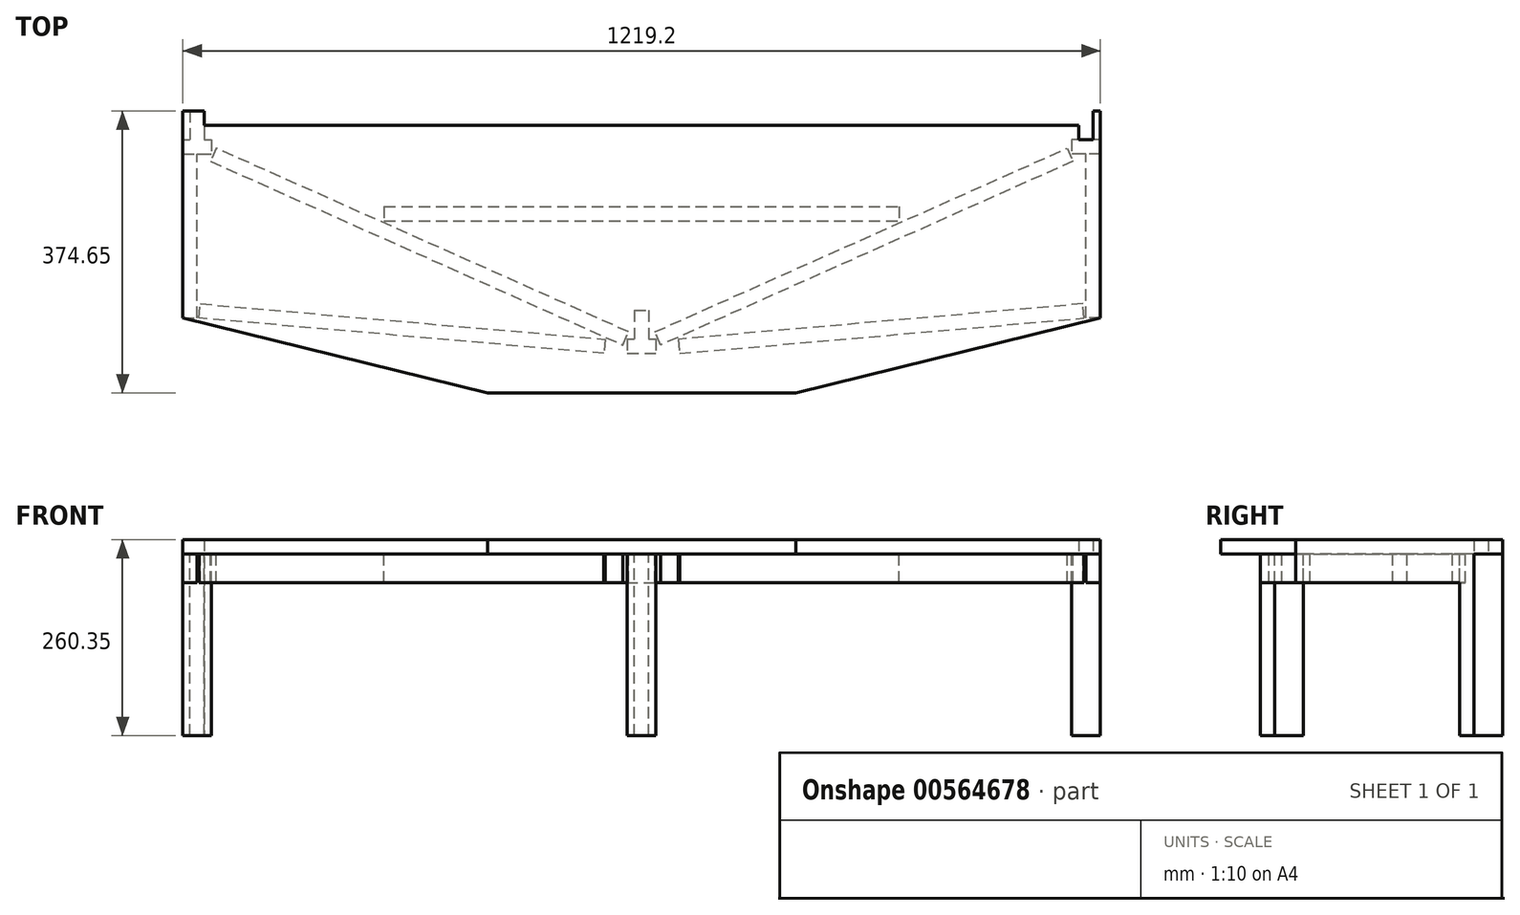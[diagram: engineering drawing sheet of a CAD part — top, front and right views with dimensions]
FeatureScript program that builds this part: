
annotation { "Feature Type Name" : "Feature", "Feature Type Description" : "" }
export const myFeature = defineFeature(function(context is Context, id is Id, definition is map)
    precondition{}
    {
        {
            var Q0;
            Q0=qCreatedBy(makeId("Top.planeOp"),FACE);
            var sketch = newSketch(context, id + "F0", { "sketchPlane" : qUnion([Q0])});
            skLineSegment(sketch, "E0", {"start": v(0, 0) * mm, "end": v(10.64, -43.16) * mm});
            skLineSegment(sketch, "E1", {"start": v(10.64, -43.16) * mm, "end": v(185.74, 0) * mm});
            skLineSegment(sketch, "E2", {"start": v(185.74, 0) * mm, "end": v(0, 0) * mm});
            skLineSegment(sketch, "E3.bottom", {"start": v(-19.05, 76.2) * mm, "end": v(19.05, 76.2) * mm});
            skLineSegment(sketch, "E3.top", {"start": v(-19.05, 57.15) * mm, "end": v(19.05, 57.15) * mm});
            skLineSegment(sketch, "E3.left", {"start": v(-19.05, 76.2) * mm, "end": v(-19.05, 57.15) * mm});
            skLineSegment(sketch, "E3.right", {"start": v(19.05, 76.2) * mm, "end": v(19.05, 57.15) * mm});
            skLineSegment(sketch, "E4", {"start": v(185.74, 0) * mm, "end": v(205.06, 4.76) * mm});
            skLineSegment(sketch, "E5", {"start": v(-237, 409.58) * mm, "end": v(373.28, 409.58) * mm});
            skPoint(sketch, "E6", {"position": v(0, -44.45) * mm});
            skLineSegment(sketch, "E7", {"start": v(205.06, 4.76) * mm, "end": v(-205.06, 4.76) * mm});
            skLineSegment(sketch, "E8", {"start": v(205.06, 4.76) * mm, "end": v(609.6, 104.47) * mm});
            skLineSegment(sketch, "E9", {"start": v(609.6, 104.47) * mm, "end": v(609.6, 379.41) * mm});
            skLineSegment(sketch, "E10.MirrorCS", {"start": v(-205.06, 4.76) * mm, "end": v(-609.6, 104.47) * mm});
            skLineSegment(sketch, "E11.MirrorCS", {"start": v(-609.6, 104.47) * mm, "end": v(-609.6, 379.41) * mm});
            skLineSegment(sketch, "E12", {"start": v(-609.6, 379.41) * mm, "end": v(609.6, 379.41) * mm});
            skLineSegment(sketch, "E13.bottom", {"start": v(609.6, 341.31) * mm, "end": v(571.5, 341.31) * mm});
            skLineSegment(sketch, "E13.top", {"start": v(609.6, 322.26) * mm, "end": v(571.5, 322.26) * mm});
            skLineSegment(sketch, "E13.left", {"start": v(609.6, 341.31) * mm, "end": v(609.6, 322.26) * mm});
            skLineSegment(sketch, "E13.right", {"start": v(571.5, 341.31) * mm, "end": v(571.5, 322.26) * mm});
            skLineSegment(sketch, "E14", {"start": v(760.84, 406.6) * mm, "end": v(1019.91, 521.99) * mm});
            skLineSegment(sketch, "E15", {"start": v(17.5, 85.93) * mm, "end": v(565.3, 329.93) * mm});
            skLineSegment(sketch, "E16", {"start": v(565.3, 329.93) * mm, "end": v(573.06, 312.53) * mm});
            skLineSegment(sketch, "E17", {"start": v(573.06, 312.53) * mm, "end": v(25.25, 68.53) * mm});
            skLineSegment(sketch, "E18", {"start": v(25.25, 68.53) * mm, "end": v(17.5, 85.93) * mm});
            skLineSegment(sketch, "E19.MirrorCS", {"start": v(-25.25, 68.53) * mm, "end": v(-17.5, 85.93) * mm});
            skLineSegment(sketch, "E20.MirrorCS", {"start": v(-17.5, 85.93) * mm, "end": v(-565.3, 329.93) * mm});
            skLineSegment(sketch, "E21.MirrorCS", {"start": v(-573.06, 312.53) * mm, "end": v(-25.25, 68.53) * mm});
            skLineSegment(sketch, "E22.MirrorCS", {"start": v(-565.3, 329.93) * mm, "end": v(-573.06, 312.53) * mm});
            skLineSegment(sketch, "E23.MirrorCS", {"start": v(-571.5, 341.31) * mm, "end": v(-571.5, 322.26) * mm});
            skLineSegment(sketch, "E24.MirrorCS", {"start": v(-609.6, 322.26) * mm, "end": v(-571.5, 322.26) * mm});
            skLineSegment(sketch, "E25.MirrorCS", {"start": v(-609.6, 341.31) * mm, "end": v(-571.5, 341.31) * mm});
            skLineSegment(sketch, "E26.MirrorCS", {"start": v(-609.6, 341.31) * mm, "end": v(-609.6, 322.26) * mm});
            skLineSegment(sketch, "E27.bottom", {"start": v(581.02, 379.41) * mm, "end": v(600.07, 379.41) * mm});
            skLineSegment(sketch, "E27.top", {"start": v(581.02, 341.31) * mm, "end": v(600.08, 341.31) * mm});
            skLineSegment(sketch, "E27.left", {"start": v(581.02, 379.41) * mm, "end": v(581.02, 341.31) * mm});
            skLineSegment(sketch, "E27.right", {"start": v(600.08, 379.41) * mm, "end": v(600.08, 341.31) * mm});
            skPoint(sketch, "E28", {"position": v(590.55, 341.31) * mm});
            skLineSegment(sketch, "E29.bottom", {"start": v(-9.52, 114.3) * mm, "end": v(9.53, 114.3) * mm});
            skLineSegment(sketch, "E29.top", {"start": v(-9.53, 76.2) * mm, "end": v(9.53, 76.2) * mm});
            skLineSegment(sketch, "E29.left", {"start": v(-9.52, 114.3) * mm, "end": v(-9.52, 76.2) * mm});
            skLineSegment(sketch, "E29.right", {"start": v(9.53, 114.3) * mm, "end": v(9.53, 76.2) * mm});
            skPoint(sketch, "E30", {"position": v(0, 76.2) * mm});
            skLineSegment(sketch, "E31.bottom", {"start": v(609.6, 104.47) * mm, "end": v(590.55, 104.47) * mm});
            skLineSegment(sketch, "E31.top", {"start": v(609.6, 322.26) * mm, "end": v(590.55, 322.26) * mm});
            skLineSegment(sketch, "E31.left", {"start": v(609.6, 104.47) * mm, "end": v(609.6, 322.26) * mm});
            skLineSegment(sketch, "E31.right", {"start": v(590.55, 104.47) * mm, "end": v(590.55, 322.26) * mm});
            skLineSegment(sketch, "E32", {"start": v(50.2, 57.15) * mm, "end": v(588.02, 104.25) * mm});
            skLineSegment(sketch, "E33", {"start": v(588.02, 104.25) * mm, "end": v(586.36, 123.23) * mm});
            skLineSegment(sketch, "E34", {"start": v(586.36, 123.23) * mm, "end": v(48.54, 76.13) * mm});
            skLineSegment(sketch, "E35", {"start": v(48.54, 76.13) * mm, "end": v(50.2, 57.15) * mm});
            skLineSegment(sketch, "E36.MirrorCS", {"start": v(-48.54, 76.13) * mm, "end": v(-50.2, 57.15) * mm});
            skLineSegment(sketch, "E37.MirrorCS", {"start": v(-586.36, 123.23) * mm, "end": v(-48.54, 76.13) * mm});
            skLineSegment(sketch, "E38.MirrorCS", {"start": v(-50.2, 57.15) * mm, "end": v(-588.02, 104.25) * mm});
            skLineSegment(sketch, "E39.MirrorCS", {"start": v(-588.02, 104.25) * mm, "end": v(-586.36, 123.23) * mm});
            skLineSegment(sketch, "E40.MirrorCS", {"start": v(-609.6, 104.47) * mm, "end": v(-590.55, 104.47) * mm});
            skLineSegment(sketch, "E41.MirrorCS", {"start": v(-590.55, 104.47) * mm, "end": v(-590.55, 322.26) * mm});
            skLineSegment(sketch, "E42.MirrorCS", {"start": v(-609.6, 322.26) * mm, "end": v(-590.55, 322.26) * mm});
            skLineSegment(sketch, "E43.MirrorCS", {"start": v(-600.08, 379.41) * mm, "end": v(-600.08, 341.31) * mm});
            skLineSegment(sketch, "E44.MirrorCS", {"start": v(-581.02, 379.41) * mm, "end": v(-600.07, 379.41) * mm});
            skLineSegment(sketch, "E45.MirrorCS", {"start": v(-581.02, 379.41) * mm, "end": v(-581.02, 341.31) * mm});
            skLineSegment(sketch, "E46.MirrorCS", {"start": v(-581.02, 341.31) * mm, "end": v(-600.08, 341.31) * mm});
            skLineSegment(sketch, "E47.bottom", {"start": v(-581.02, 379.41) * mm, "end": v(581.02, 379.41) * mm});
            skLineSegment(sketch, "E47.top", {"start": v(-581.02, 360.36) * mm, "end": v(581.02, 360.36) * mm});
            skLineSegment(sketch, "E47.left", {"start": v(-581.02, 379.41) * mm, "end": v(-581.02, 360.36) * mm});
            skLineSegment(sketch, "E47.right", {"start": v(581.02, 379.41) * mm, "end": v(581.02, 360.36) * mm});
            skLineSegment(sketch, "E48.bottom", {"start": v(-342.25, 252.41) * mm, "end": v(342.25, 252.41) * mm});
            skLineSegment(sketch, "E48.top", {"start": v(-342.25, 233.36) * mm, "end": v(342.25, 233.36) * mm});
            skLineSegment(sketch, "E48.left", {"start": v(-342.25, 252.41) * mm, "end": v(-342.25, 233.36) * mm});
            skLineSegment(sketch, "E48.right", {"start": v(342.25, 252.41) * mm, "end": v(342.25, 233.36) * mm});
            skSolve(sketch);
        }
        {
            var Q0;
            Q0=makeQuery(id+"F0.imprint","IMPRINT",FACE,{"disambiguationData":[TD([[makeQuery(id+"F0.imprint","IMPRINT",EDGE,{"derivedFrom":sQuery(id+"F0.wireOp",EDGE,"E3.top")}),-1.0]])]});
            var Q1;
            Q1=makeQuery(id+"F0.imprint","IMPRINT",FACE,{"disambiguationData":[TD([[makeQuery(id+"F0.imprint","IMPRINT",EDGE,{"derivedFrom":sQuery(id+"F0.wireOp",EDGE,"E13.bottom")}),1.0]])]});
            var Q2;
            {var subQ3=sQuery(id+"F0.wireOp",EDGE,"E15");Q2=makeQuery(id+"F0.imprint","IMPRINT",FACE,{"disambiguationData":[TD([[makeQuery(id+"F0.imprint","IMPRINT",EDGE,{"derivedFrom":subQ3}),-1.0]])]});}
            var Q3;
            Q3=makeQuery(id+"F0.imprint","IMPRINT",FACE,{"disambiguationData":[TD([[makeQuery(id+"F0.imprint","IMPRINT",EDGE,{"derivedFrom":sQuery(id+"F0.wireOp",EDGE,"E3.bottom")}),-1.0]])]});
            var Q4;
            {var subQ1=sQuery(id+"F0.wireOp",EDGE,"E20.MirrorCS");Q4=makeQuery(id+"F0.imprint","IMPRINT",FACE,{"disambiguationData":[TD([[makeQuery(id+"F0.imprint","IMPRINT",EDGE,{"derivedFrom":subQ1}),1.0]])]});}
            var Q5;
            Q5=makeQuery(id+"F0.imprint","IMPRINT",FACE,{"disambiguationData":[TD([[makeQuery(id+"F0.imprint","IMPRINT",EDGE,{"derivedFrom":sQuery(id+"F0.wireOp",EDGE,"E23.MirrorCS")}),-1.0]])]});
            var Q6;
            {var subQ5=sQuery(id+"F0.wireOp",EDGE,"E3.bottom");Q6=makeQuery(id+"F0.imprint","IMPRINT",FACE,{"disambiguationData":[TD([[makeQuery(id+"F0.imprint","IMPRINT",EDGE,{"derivedFrom":subQ5}),1.0]])]});}
            var Q7;
            {var subQ5=sQuery(id+"F0.wireOp",EDGE,"E43.MirrorCS");Q7=makeQuery(id+"F0.imprint","IMPRINT",FACE,{"disambiguationData":[TD([[makeQuery(id+"F0.imprint","IMPRINT",EDGE,{"derivedFrom":subQ5}),-1.0]])]});}
            var Q8;
            Q8=makeQuery(id+"F0.imprint","IMPRINT",FACE,{"disambiguationData":[TD([[makeQuery(id+"F0.imprint","IMPRINT",EDGE,{"derivedFrom":sQuery(id+"F0.wireOp",EDGE,"E43.MirrorCS")}),1.0]])]});
            var Q9;
            Q9=makeQuery(id+"F0.imprint","IMPRINT",FACE,{"disambiguationData":[TD([[makeQuery(id+"F0.imprint","IMPRINT",EDGE,{"derivedFrom":sQuery(id+"F0.wireOp",EDGE,"E47.bottom")}),-1.0]])]});
            var Q10;
            {var subQ0=sQuery(id+"F0.wireOp",EDGE,"E40.MirrorCS");Q10=makeQuery(id+"F0.imprint","IMPRINT",FACE,{"disambiguationData":[TD([[makeQuery(id+"F0.imprint","IMPRINT",EDGE,{"derivedFrom":subQ0}),1.0]])]});}
            var Q11;
            {var subQ4=sQuery(id+"F0.wireOp",EDGE,"E24.MirrorCS");Q11=makeQuery(id+"F0.imprint","IMPRINT",FACE,{"disambiguationData":[TD([[makeQuery(id+"F0.imprint","IMPRINT",EDGE,{"derivedFrom":subQ4}),-1.0]])]});}
            var Q12;
            Q12=makeQuery(id+"F0.imprint","IMPRINT",FACE,{"disambiguationData":[TD([[makeQuery(id+"F0.imprint","IMPRINT",EDGE,{"derivedFrom":sQuery(id+"F0.wireOp",EDGE,"E36.MirrorCS")}),-1.0]])]});
            var Q13;
            Q13=makeQuery(id+"F0.imprint","IMPRINT",FACE,{"disambiguationData":[TD([[makeQuery(id+"F0.imprint","IMPRINT",EDGE,{"derivedFrom":sQuery(id+"F0.wireOp",EDGE,"E29.bottom")}),-1.0]])]});
            var Q14;
            Q14=makeQuery(id+"F0.imprint","IMPRINT",FACE,{"disambiguationData":[TD([[makeQuery(id+"F0.imprint","IMPRINT",EDGE,{"derivedFrom":sQuery(id+"F0.wireOp",EDGE,"E32")}),1.0]])]});
            var Q15;
            {var subQ0=sQuery(id+"F0.wireOp",EDGE,"E13.top");Q15=makeQuery(id+"F0.imprint","IMPRINT",FACE,{"disambiguationData":[TD([[makeQuery(id+"F0.imprint","IMPRINT",EDGE,{"derivedFrom":subQ0}),1.0]])]});}
            var Q16;
            Q16=makeQuery(id+"F0.imprint","IMPRINT",FACE,{"disambiguationData":[TD([[makeQuery(id+"F0.imprint","IMPRINT",EDGE,{"derivedFrom":sQuery(id+"F0.wireOp",EDGE,"E31.bottom")}),-1.0]])]});
            var Q17;
            Q17=makeQuery(id+"F0.imprint","IMPRINT",FACE,{"disambiguationData":[TD([[makeQuery(id+"F0.imprint","IMPRINT",EDGE,{"derivedFrom":sQuery(id+"F0.wireOp",EDGE,"E27.bottom")}),-1.0]])]});
            var Q18;
            {var subQ0=sQuery(id+"F0.wireOp",EDGE,"E9");Q18=makeQuery(id+"F0.imprint","IMPRINT",FACE,{"disambiguationData":[TD([[makeQuery(id+"F0.imprint","IMPRINT",EDGE,{"derivedFrom":subQ0}),1.0]])]});}
            var Q19;
            Q19=makeQuery(id+"F0.imprint","IMPRINT",FACE,{"disambiguationData":[TD([[makeQuery(id+"F0.imprint","IMPRINT",EDGE,{"derivedFrom":sQuery(id+"F0.wireOp",EDGE,"E48.bottom")}),-1.0]])]});
            extrude(context, id + "F1", {"entities" : qUnion([Q0, Q1, Q2, Q3, Q4, Q5, Q6, Q7, Q8, Q9, Q10, Q11, Q12, Q13, Q14, Q15, Q16, Q17, Q18, Q19]), "depth" : 19.05 * mm, "offsetDistance" : 25.4 * mm});
        }
        {
            var Q0;
            {var subQ1=sQuery(id+"F0.wireOp",EDGE,"E23.MirrorCS");Q0=makeQuery(id+"F0.imprint","IMPRINT",FACE,{"disambiguationData":[TD([[makeQuery(id+"F0.imprint","IMPRINT",EDGE,{"derivedFrom":subQ1}),-1.0]])]});}
            var Q1;
            Q1=makeQuery(id+"F0.imprint","IMPRINT",FACE,{"disambiguationData":[TD([[makeQuery(id+"F0.imprint","IMPRINT",EDGE,{"derivedFrom":sQuery(id+"F0.wireOp",EDGE,"E3.top")}),1.0]])]});
            var Q2;
            Q2=makeQuery(id+"F0.imprint","IMPRINT",FACE,{"disambiguationData":[TD([[makeQuery(id+"F0.imprint","IMPRINT",EDGE,{"derivedFrom":sQuery(id+"F0.wireOp",EDGE,"E13.top")}),-1.0]])]});
            var Q3;
            Q3=makeQuery(id+"F0.imprint","IMPRINT",FACE,{"disambiguationData":[TD([[makeQuery(id+"F0.imprint","IMPRINT",EDGE,{"derivedFrom":sQuery(id+"F0.wireOp",EDGE,"E27.bottom")}),-1.0]])]});
            var Q4;
            Q4=makeQuery(id+"F0.imprint","IMPRINT",FACE,{"disambiguationData":[TD([[makeQuery(id+"F0.imprint","IMPRINT",EDGE,{"derivedFrom":sQuery(id+"F0.wireOp",EDGE,"E29.bottom")}),-1.0]])]});
            var Q5;
            Q5=makeQuery(id+"F0.imprint","IMPRINT",FACE,{"disambiguationData":[TD([[makeQuery(id+"F0.imprint","IMPRINT",EDGE,{"derivedFrom":sQuery(id+"F0.wireOp",EDGE,"E43.MirrorCS")}),1.0]])]});
            extrude(context, id + "F2", {"entities" : qUnion([Q0, Q1, Q2, Q3, Q4, Q5]), "operationType" : NewBodyOperationType.ADD, "oppositeDirection" : true, "depth" : 241.3 * mm, "offsetDistance" : 25.4 * mm});
        }
        {
            var Q0;
            {var subQ0=sQuery(id+"F0.wireOp",EDGE,"E40.MirrorCS");Q0=makeQuery(id+"F0.imprint","IMPRINT",FACE,{"disambiguationData":[TD([[makeQuery(id+"F0.imprint","IMPRINT",EDGE,{"derivedFrom":subQ0}),1.0]])]});}
            var Q1;
            Q1=makeQuery(id+"F0.imprint","IMPRINT",FACE,{"disambiguationData":[TD([[makeQuery(id+"F0.imprint","IMPRINT",EDGE,{"derivedFrom":sQuery(id+"F0.wireOp",EDGE,"E36.MirrorCS")}),-1.0]])]});
            var Q2;
            {var subQ4=sQuery(id+"F0.wireOp",EDGE,"E20.MirrorCS");Q2=makeQuery(id+"F0.imprint","IMPRINT",FACE,{"disambiguationData":[TD([[makeQuery(id+"F0.imprint","IMPRINT",EDGE,{"derivedFrom":subQ4}),1.0]])]});}
            var Q3;
            Q3=makeQuery(id+"F0.imprint","IMPRINT",FACE,{"disambiguationData":[TD([[makeQuery(id+"F0.imprint","IMPRINT",EDGE,{"derivedFrom":sQuery(id+"F0.wireOp",EDGE,"E47.bottom")}),-1.0]])]});
            var Q4;
            {var subQ5=sQuery(id+"F0.wireOp",EDGE,"E15");Q4=makeQuery(id+"F0.imprint","IMPRINT",FACE,{"disambiguationData":[TD([[makeQuery(id+"F0.imprint","IMPRINT",EDGE,{"derivedFrom":subQ5}),-1.0]])]});}
            var Q5;
            Q5=makeQuery(id+"F0.imprint","IMPRINT",FACE,{"disambiguationData":[TD([[makeQuery(id+"F0.imprint","IMPRINT",EDGE,{"derivedFrom":sQuery(id+"F0.wireOp",EDGE,"E31.bottom")}),-1.0]])]});
            var Q6;
            Q6=makeQuery(id+"F0.imprint","IMPRINT",FACE,{"disambiguationData":[TD([[makeQuery(id+"F0.imprint","IMPRINT",EDGE,{"derivedFrom":sQuery(id+"F0.wireOp",EDGE,"E32")}),1.0]])]});
            var Q7;
            Q7=makeQuery(id+"F0.imprint","IMPRINT",FACE,{"disambiguationData":[TD([[makeQuery(id+"F0.imprint","IMPRINT",EDGE,{"derivedFrom":sQuery(id+"F0.wireOp",EDGE,"E48.bottom")}),-1.0]])]});
            extrude(context, id + "F3", {"entities" : qUnion([Q0, Q1, Q2, Q3, Q4, Q5, Q6, Q7]), "operationType" : NewBodyOperationType.ADD, "oppositeDirection" : true, "depth" : 38.1 * mm, "offsetDistance" : 25.4 * mm});
        }
    });
